# Revit family: ThinkingWall Combi AV
name_source: partatom
category: Generic Models
units: mm (PartAtom-declared; Revit-internal decimal feet)

## family parameters
Always vertical = Yes
Can host rebar = No
Cut with Voids When Loaded = No
Maintain Annotation Orientation = No
Part Type = Normal
Room Calculation Point = No
Round Connector Dimension = Use Diameter
Shared = No
Work Plane-Based = No

## types (2) — shared parameters
Acoustic Colour = <By Category>
Cupboard Colour = <By Category>
Description = Mobile freestanding storage unit with integrated screen and AV equipment. Part of the ThinkingWall® range for flexible breakout and meeting spaces.
Manufacturer = Logovisual LTD
Model = ThinkingWall® Combi AV
Plinth Colure = <By Category>
Steel Colour = <By Category>
TV Screen Colour = Screen
URL = https://www.logovisual.com
zero-valued in all types: Default Elevation

## per-type parameters (varying)
| type | TV Height | TV Width | ThinkingWall Combi AV 1200 | ThinkingWall Combi AV 1500 |
| ThinkingWall® Combi AV 1200 | 565 mm  [stored 1.85367 ft] | 965 mm  [stored 3.16601 ft] | Yes | No |
| ThinkingWall® Combi AV 1500 | 720 mm  [stored 2.3622 ft] | 1230 mm  [stored 4.03543 ft] | No | Yes |

note: [stored X ft] marks values corroborated as IEEE doubles in the binary element streams (Revit-internal decimal feet)

## geometry (parser evidence)
native form markers: Sweep x39
no freeform markers — native parametric forms only
